# Revit family: Seating_Inc-EDU2_Guest
name_source: partatom
category: Furniture
revit_build: Autodesk Revit 2014 (Build: 20130308_1515(x64)
units: mm (PartAtom-declared; Revit-internal decimal feet)

## types (2) — shared parameters
Arm Finish = STI - Plastic Black
Assembly Code = E2020200
Back Finish = STI - Leather
Glide Finish = STI - Plastic Black
Keynote = 12500
Leg Finish = STI - Power Coat - Black
Low Emitting Finish = Yes
Low Emitting Material = Yes
Manufacturer = Seating Inc
Plastic Finish = STI - Plastic Black
Salvage or Reuse = Yes
Seat Finish = STI - Leather
Type Comments = Quick Configuration
URL = www.seatinginc.com
zero-valued in all types: Percentage of Recycled Content

## per-type parameters (varying)
| type | Arm V | Depth | Description | Height | Width |
| Q-3ES43-A | No | 24 1/2" | EDU2 Guest Guest Armless 20.5W x 24.5D x 32H | 32" | 20 1/2" |
| Q-3ES44-B | Yes | 23 3/4" | EDU2 Guest Guest with Arms  24.5W x 24.75D x 31.5H | 31 1/2" | 24 1/2" |

note: column(s) folded — value = type name in every type: Model

## geometry (parser evidence)
native form markers: Sweep x4
no freeform markers — native parametric forms only
